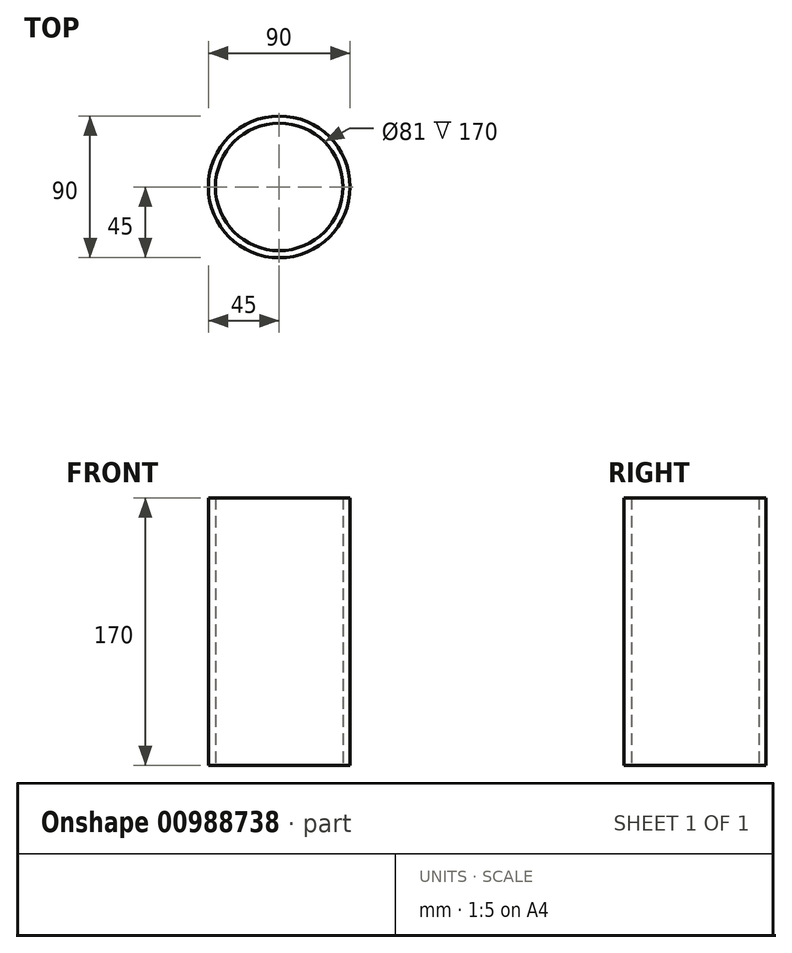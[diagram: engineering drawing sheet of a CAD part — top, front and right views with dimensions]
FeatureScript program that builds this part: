
annotation { "Feature Type Name" : "Feature", "Feature Type Description" : "" }
export const myFeature = defineFeature(function(context is Context, id is Id, definition is map)
    precondition{}
    {
        {
            var Q0;
            Q0=qCreatedBy(makeId("Top.planeOp"),FACE);
            var sketch = newSketch(context, id + "F0", { "sketchPlane" : qUnion([Q0])});
            skCircle(sketch, "E0", {"center": v(0, 0) * mm, "radius": 45 * mm});
            skCircle(sketch, "E1", {"center": v(0, 0) * mm, "radius": 40.5 * mm});
            skSolve(sketch);
        }
        {
            var Q0;
            Q0=makeQuery(id+"F0.imprint","IMPRINT",FACE,{"disambiguationData":[TD([[makeQuery(id+"F0.imprint","IMPRINT",EDGE,{"derivedFrom":sQuery(id+"F0.wireOp",EDGE,"E0")}),1.0]])]});
            extrude(context, id + "F1", {"entities" : qUnion([Q0]), "depth" : 170 * mm, "offsetDistance" : 25 * mm});
        }
    });
